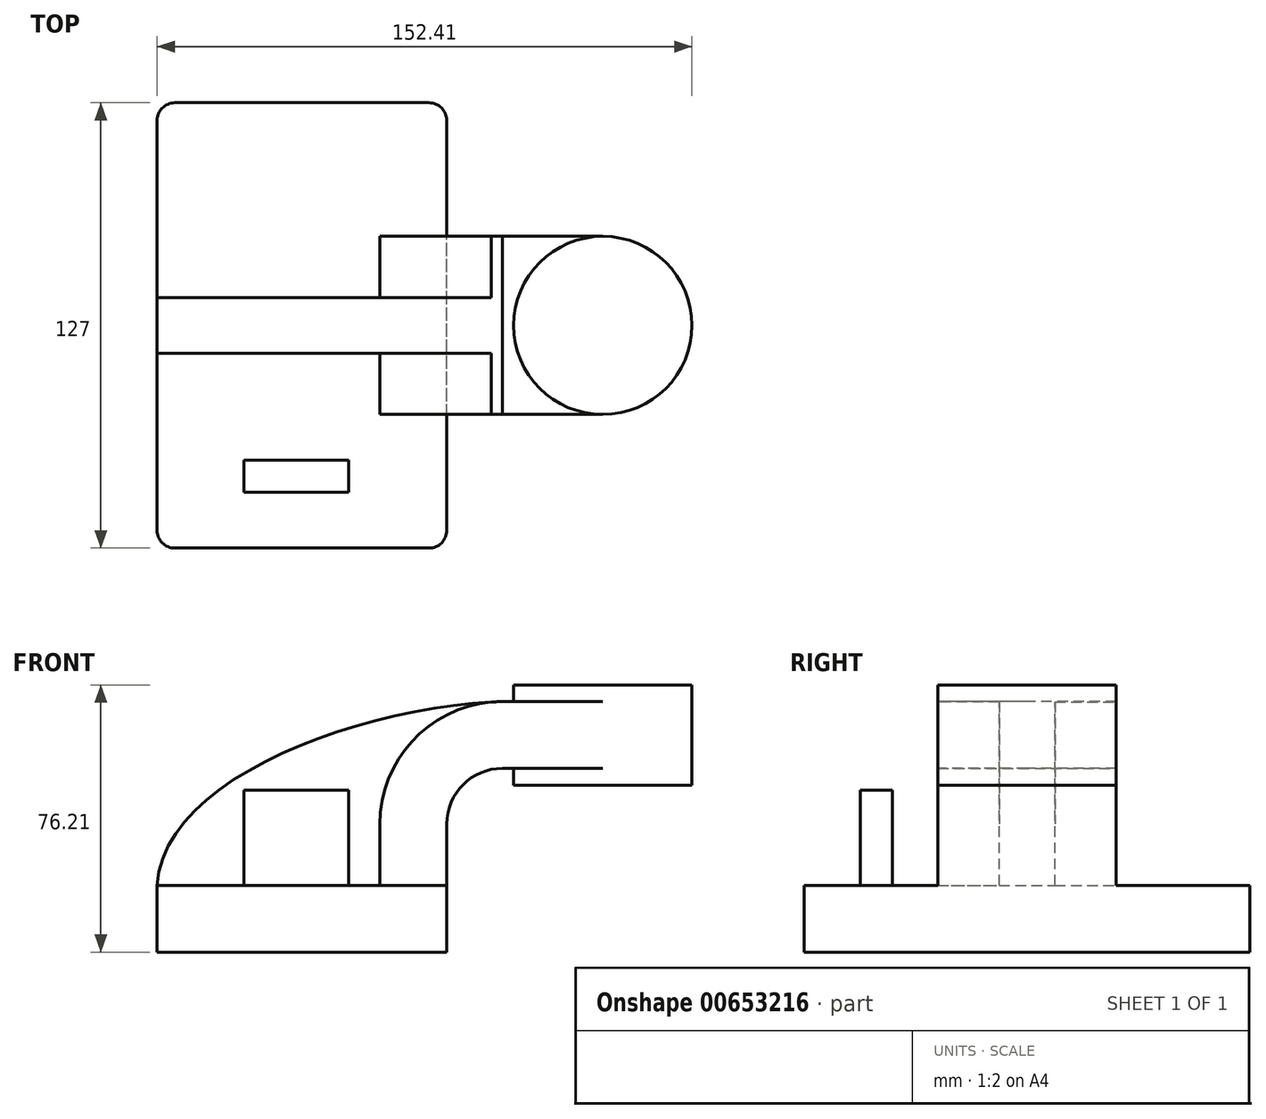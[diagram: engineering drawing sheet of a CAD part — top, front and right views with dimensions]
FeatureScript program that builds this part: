
annotation { "Feature Type Name" : "Feature", "Feature Type Description" : "" }
export const myFeature = defineFeature(function(context is Context, id is Id, definition is map)
    precondition{}
    {
        {
            var Q0;
            Q0=qCreatedBy(makeId("Front.planeOp"),FACE);
            var sketch = newSketch(context, id + "F0", { "sketchPlane" : qUnion([Q0])});
            skLineSegment(sketch, "E0.rect.bottom", {"start": v(-41.28, 9.52) * mm, "end": v(41.28, 9.52) * mm});
            skLineSegment(sketch, "E0.rect.top", {"start": v(-41.28, -9.52) * mm, "end": v(41.28, -9.52) * mm});
            skLineSegment(sketch, "E0.rect.left", {"start": v(-41.28, 9.52) * mm, "end": v(-41.28, -9.52) * mm});
            skLineSegment(sketch, "E0.rect.right", {"start": v(41.28, 9.52) * mm, "end": v(41.28, -9.52) * mm});
            skPoint(sketch, "E0.rect.middle", {"position": v(0, 0) * mm});
            skLineSegment(sketch, "E1", {"start": v(41.28, 9.52) * mm, "end": v(41.28, 27) * mm});
            skArc(sketch, "E2", {"start": v(41.28, 27) * mm, "mid": v(45.92, 38.23) * mm, "end": v(57.15, 42.88) * mm});
            skLineSegment(sketch, "E3", {"start": v(57.15, 42.88) * mm, "end": v(85.72, 42.88) * mm});
            skLineSegment(sketch, "E4.rect.bottom", {"start": v(60.32, 38.1) * mm, "end": v(111.12, 38.1) * mm});
            skLineSegment(sketch, "E4.rect.top", {"start": v(60.32, 66.68) * mm, "end": v(111.12, 66.68) * mm});
            skLineSegment(sketch, "E4.rect.left", {"start": v(60.32, 38.1) * mm, "end": v(60.32, 66.68) * mm});
            skLineSegment(sketch, "E4.rect.right", {"start": v(111.13, 38.1) * mm, "end": v(111.12, 66.68) * mm});
            skPoint(sketch, "E4.rect.middle", {"position": v(85.72, 52.39) * mm});
            skLineSegment(sketch, "E5.0", {"start": v(57.15, 61.93) * mm, "end": v(85.72, 61.93) * mm});
            skArc(sketch, "E5.1", {"start": v(22.23, 27) * mm, "mid": v(32.45, 51.7) * mm, "end": v(57.15, 61.93) * mm});
            skLineSegment(sketch, "E5.2", {"start": v(22.23, 9.52) * mm, "end": v(22.23, 27) * mm});
            skLineSegment(sketch, "E6", {"start": v(85.72, 38.1) * mm, "end": v(85.72, 66.68) * mm});
            skFitSpline(sketch, "E7", {"points": [v(-41.28, 9.53) * mm, v(57.15, 61.93) * mm], "startDerivative": vector(5.2, 92.34) * mm, "endDerivative": vector(120.92, 4.22) * mm});
            skSolve(sketch);
        }
        {
            var Q0;
            Q0=makeQuery(id+"F0.imprint","IMPRINT",FACE,{"disambiguationData":[TD([[makeQuery(id+"F0.imprint","IMPRINT",EDGE,{"derivedFrom":sQuery(id+"F0.wireOp",EDGE,"E0.rect.top")}),1.0]])]});
            extrude(context, id + "F1", {"entities" : qUnion([Q0]), "endBound" : BoundingType.SYMMETRIC, "depth" : 127 * mm});
        }
        {
            var Q0;
            {var subQ9=sQuery(id+"F0.wireOp",EDGE,"E1");Q0=makeQuery(id+"F0.imprint","IMPRINT",FACE,{"disambiguationData":[TD([[makeQuery(id+"F0.imprint","IMPRINT",EDGE,{"derivedFrom":subQ9}),1.0]])]});}
            var Q1;
            {var subQ0=sQuery(id+"F0.wireOp",EDGE,"E6");var subQ1=sQuery(id+"F0.wireOp",EDGE,"E3");var subQ2=makeQuery(id+"F0.imprint","INTERSECT",VERTEX,{"derivedFrom":[subQ1,subQ0]});Q1=makeQuery(id+"F0.imprint","IMPRINT",FACE,{"disambiguationData":[TD([[makeQuery(id+"F0.imprint","IMPRINT",EDGE,{"disambiguationData":[TD([[subQ2,1.0]])],"derivedFrom":subQ1}),1.0]])]});}
            extrude(context, id + "F2", {"entities" : qUnion([Q0, Q1]), "operationType" : NewBodyOperationType.ADD, "endBound" : BoundingType.SYMMETRIC, "depth" : 50.8 * mm});
        }
        {
            var Q0;
            {var subQ3=sQuery(id+"F0.wireOp",EDGE,"E5.2");Q0=makeQuery(id+"F0.imprint","IMPRINT",FACE,{"disambiguationData":[TD([[makeQuery(id+"F0.imprint","IMPRINT",EDGE,{"derivedFrom":subQ3}),1.0]])]});}
            extrude(context, id + "F3", {"entities" : qUnion([Q0]), "operationType" : NewBodyOperationType.ADD, "endBound" : BoundingType.SYMMETRIC, "depth" : 15.88 * mm});
        }
        {
            var Q0;
            {var subQ5=sQuery(id+"F0.wireOp",EDGE,"E4.rect.right");Q0=makeQuery(id+"F0.imprint","IMPRINT",FACE,{"disambiguationData":[TD([[makeQuery(id+"F0.imprint","IMPRINT",EDGE,{"derivedFrom":subQ5}),1.0]])]});}
            var Q1;
            Q1=sQuery(id+"F0.wireOp",EDGE,"E6");
            revolve(context, id + "F4", {"operationType" : NewBodyOperationType.ADD, "entities" : qUnion([Q0]), "axis" : qUnion([Q1]), "revolveType" : RevolveType.FULL});
        }
        {
            var Q0;
            Q0=makeQuery(id+"F1.opExtrude","CAP_EDGE",EDGE,{"disambiguationData":[OSD([sQuery(id+"F0.wireOp",EDGE,"E0.rect.right")])],"isStart":false});
            var Q1;
            Q1=makeQuery(id+"F1.opExtrude","CAP_EDGE",EDGE,{"disambiguationData":[OSD([sQuery(id+"F0.wireOp",EDGE,"E0.rect.left")])],"isStart":false});
            var Q2;
            Q2=makeQuery(id+"F1.opExtrude","CAP_EDGE",EDGE,{"disambiguationData":[OSD([sQuery(id+"F0.wireOp",EDGE,"E0.rect.right")])],"isStart":true});
            var Q3;
            Q3=makeQuery(id+"F1.opExtrude","CAP_EDGE",EDGE,{"disambiguationData":[OSD([sQuery(id+"F0.wireOp",EDGE,"E0.rect.left")])],"isStart":true});
            fillet(context, id + "F5", {"entities" : qUnion([Q0, Q1, Q2, Q3]), "radius" : 5.08 * mm, "tangentPropagation" : true, "allowEdgeOverflow" : false});
        }
        {
            var Q0;
            {var subQ4=sQuery(id+"F0.wireOp",EDGE,"E0.rect.bottom");var subQ5=sQuery(id+"F0.wireOp",EDGE,"E0.rect.right");var subQ6=sQuery(id+"F0.wireOp",EDGE,"E0.rect.left");Q0=makeQuery(id+"F3.boolean.opBoolean","SPLIT",FACE,{"disambiguationData":[TD([makeQuery(id+"F1.opExtrude","CAP_FACE",FACE,{"disambiguationData":[OSD([subQ4,sQuery(id+"F0.wireOp",EDGE,"E0.rect.top"),subQ6,subQ5])],"isStart":false})])],"derivedFrom":makeQuery(id+"F1.opExtrude","SWEPT_FACE",FACE,{"disambiguationData":[OSD([subQ4])]})});}
            var sketch = newSketch(context, id + "F6", { "sketchPlane" : qUnion([Q0])});
            skLineSegment(sketch, "E8.bottom", {"start": v(-16.5, -38.41) * mm, "end": v(13.31, -38.41) * mm});
            skLineSegment(sketch, "E8.top", {"start": v(-16.5, -47.5) * mm, "end": v(13.31, -47.5) * mm});
            skLineSegment(sketch, "E8.left", {"start": v(-16.5, -38.41) * mm, "end": v(-16.5, -47.5) * mm});
            skLineSegment(sketch, "E8.right", {"start": v(13.31, -38.41) * mm, "end": v(13.31, -47.5) * mm});
            skSolve(sketch);
        }
        {
            var Q0;
            Q0=makeQuery(id+"F6.imprint","IMPRINT",FACE,{"disambiguationData":[TD([[makeQuery(id+"F6.imprint","IMPRINT",EDGE,{"derivedFrom":sQuery(id+"F6.wireOp",EDGE,"E8.bottom")}),-1.0]])]});
            extrude(context, id + "F7", {"entities" : qUnion([Q0]), "operationType" : NewBodyOperationType.ADD, "depth" : 27.18 * mm, "offsetDistance" : 25.4 * mm});
        }
    });
